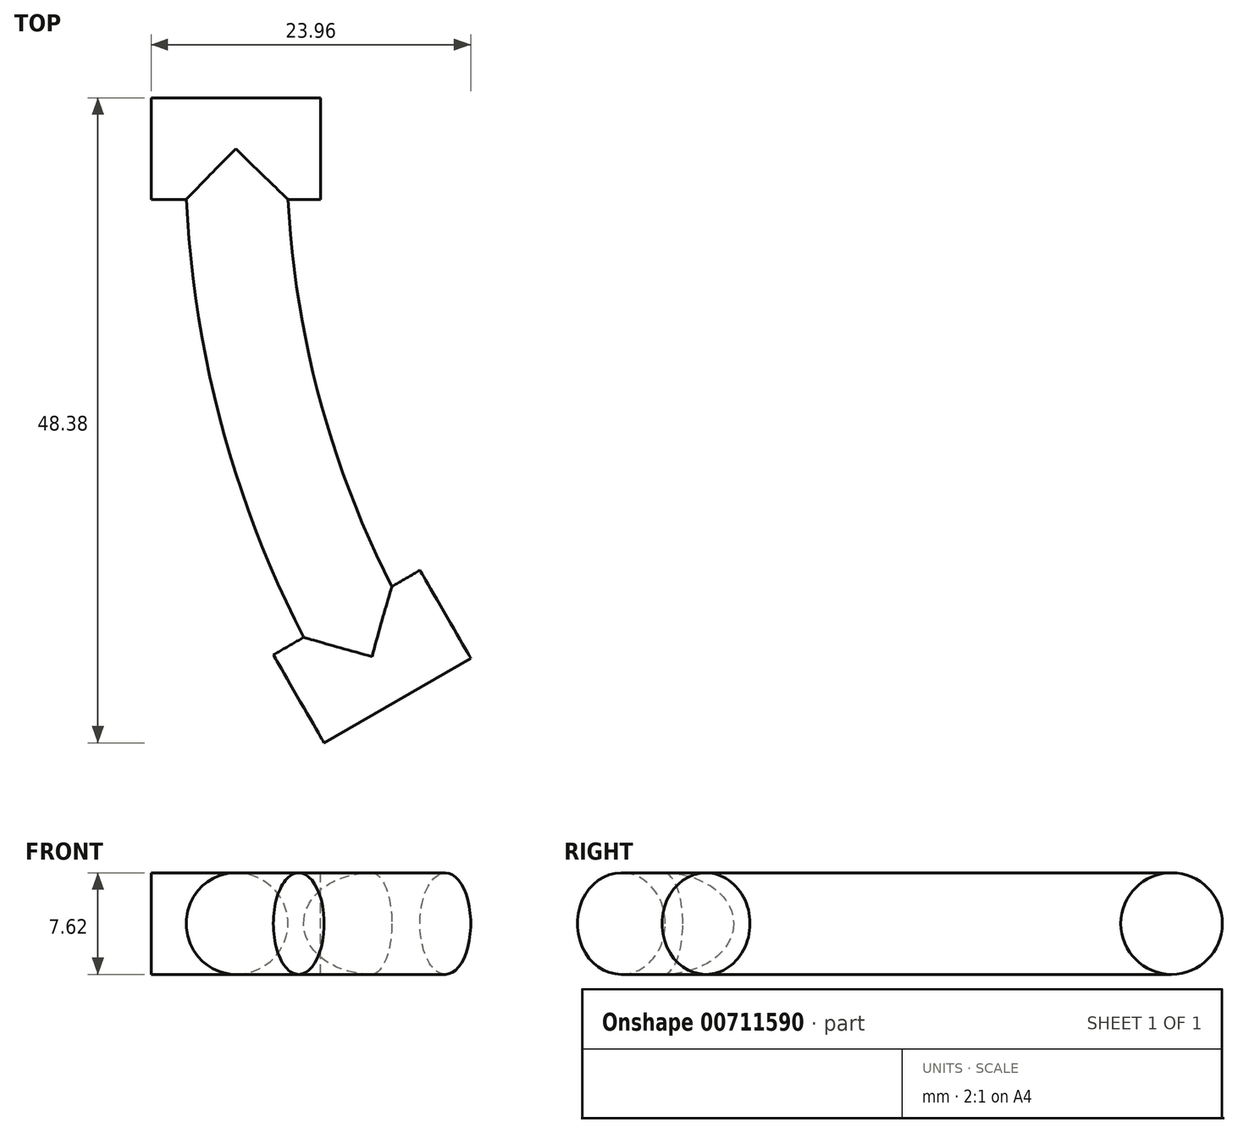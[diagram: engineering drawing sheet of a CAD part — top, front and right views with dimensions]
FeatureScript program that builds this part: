
annotation { "Feature Type Name" : "Feature", "Feature Type Description" : "" }
export const myFeature = defineFeature(function(context is Context, id is Id, definition is map)
    precondition{}
    {
        {
            var Q0;
            Q0=qCreatedBy(makeId("Front.planeOp"),FACE);
            var sketch = newSketch(context, id + "F0", { "sketchPlane" : qUnion([Q0])});
            skCircle(sketch, "E0", {"center": v(0, 0) * mm, "radius": 3.81 * mm});
            skSolve(sketch);
        }
        {
            var Q0;
            Q0=qCreatedBy(makeId("Top.planeOp"),FACE);
            var sketch = newSketch(context, id + "F1", { "sketchPlane" : qUnion([Q0])});
            skArc(sketch, "E1", {"start": v(0, 0) * mm, "mid": v(2.6, -19.72) * mm, "end": v(10.2, -38.1) * mm});
            skLineSegment(sketch, "E2", {"start": v(10.2, -38.1) * mm, "end": v(76.2, 0) * mm, "construction": true});
            skSolve(sketch);
        }
        {
            var Q0;
            Q0 = qSketchRegion(id + "F0", true);
            var Q1;
            Q1 = qConstructionFilter(qBodyType(qCreatedBy(id + "F1" ,EDGE), BodyType.WIRE), ConstructionObject.NO);
            sweep(context, id + "F2", {"profiles" : qUnion([Q0]), "path" : qUnion([Q1])});
        }
        {
            var Q0;
            Q0=qCreatedBy(makeId("Right.planeOp"),FACE);
            var sketch = newSketch(context, id + "F3", { "sketchPlane" : qUnion([Q0])});
            skCircle(sketch, "E3", {"center": v(0, 0) * mm, "radius": 3.81 * mm});
            skSolve(sketch);
        }
        {
            var Q0;
            Q0=makeQuery(id+"F3.imprint","IMPRINT",FACE,{"disambiguationData":[TD([[makeQuery(id+"F3.imprint","IMPRINT",EDGE,{"derivedFrom":sQuery(id+"F3.wireOp",EDGE,"E3")}),1.0]])]});
            var Q1;
            Q1=sQuery(id+"F3.wireOp",EDGE,"E3");
            extrude(context, id + "F4", {"entities" : qUnion([Q0]), "operationType" : NewBodyOperationType.ADD, "surfaceEntities" : qUnion([Q1]), "endBound" : BoundingType.SYMMETRIC, "depth" : 12.7 * mm, "offsetDistance" : 25.4 * mm});
        }
        {
            var Q0;
            Q0=makeQuery(id+"F2.opSweep","CAP_FACE",FACE,{"disambiguationData":[OSD([sQuery(id+"F0.wireOp",EDGE,"E0"),sQuery(id+"F1.wireOp",VERTEX,"E1.end")])],"isStart":false});
            var sketch = newSketch(context, id + "F5", { "sketchPlane" : qUnion([Q0])});
            skLineSegment(sketch, "E4", {"start": v(-10.2, 3.81) * mm, "end": v(-10.2, -3.81) * mm});
            skSolve(sketch);
        }
        {
            var Q0;
            Q0=sQuery(id+"F5.wireOp",EDGE,"E4");
            var Q1;
            {var subQ0=sQuery(id+"F5.wireOp",EDGE,"E4");Q1=makeQuery(id+"F5.imprint","IMPRINT",FACE,{"disambiguationData":[TD([[makeQuery(id+"F5.imprint","IMPRINT",EDGE,{"derivedFrom":subQ0}),1.0]])]});}
            cPlane(context, id + "F6", {"entities" : qUnion([Q0, Q1]), "cplaneType" : CPlaneType.LINE_ANGLE, "offset" : 25.4 * mm, "angle" : 90 * degree, "width" : 152.4 * mm, "height" : 152.4 * mm});
        }
        {
            var Q0;
            Q0=qCreatedBy(id+"F6.planeOp",FACE);
            var sketch = newSketch(context, id + "F7", { "sketchPlane" : qUnion([Q0])});
            skCircle(sketch, "E5", {"center": v(-38.1, 0) * mm, "radius": 3.8 * mm});
            skSolve(sketch);
        }
        {
            var Q0;
            Q0=makeQuery(id+"F7.imprint","IMPRINT",FACE,{"disambiguationData":[TD([[makeQuery(id+"F7.imprint","IMPRINT",EDGE,{"derivedFrom":sQuery(id+"F7.wireOp",EDGE,"E5")}),1.0]])]});
            extrude(context, id + "F8", {"entities" : qUnion([Q0]), "operationType" : NewBodyOperationType.ADD, "endBound" : BoundingType.SYMMETRIC, "depth" : 12.7 * mm, "offsetDistance" : 25.4 * mm});
        }
    });
